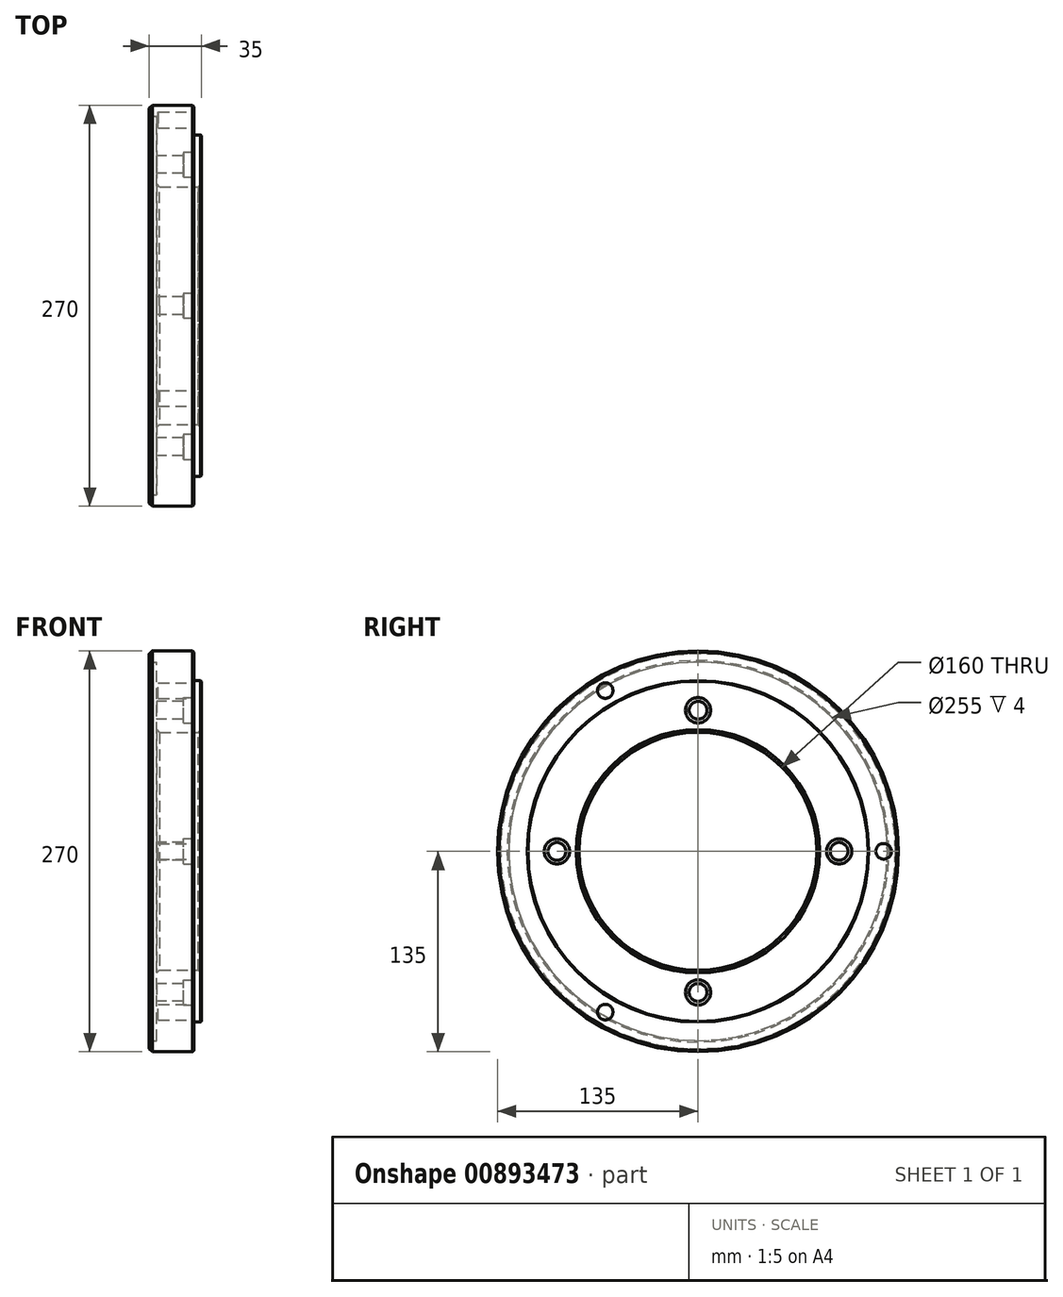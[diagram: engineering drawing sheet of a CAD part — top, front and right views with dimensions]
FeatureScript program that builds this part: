
annotation { "Feature Type Name" : "Feature", "Feature Type Description" : "" }
export const myFeature = defineFeature(function(context is Context, id is Id, definition is map)
    precondition{}
    {
        {
            var Q0;
            Q0=qCreatedBy(makeId("Top.planeOp"),FACE);
            var sketch = newSketch(context, id + "F0", { "sketchPlane" : qUnion([Q0])});
            skLineSegment(sketch, "E0", {"start": v(0, 0) * mm, "end": v(-84.67, 0) * mm, "construction": true});
            skLineSegment(sketch, "E1", {"start": v(0, 80) * mm, "end": v(0, 115) * mm});
            skLineSegment(sketch, "E2", {"start": v(0, 115) * mm, "end": v(-5, 115) * mm});
            skLineSegment(sketch, "E3", {"start": v(-5, 115) * mm, "end": v(-5, 135) * mm});
            skLineSegment(sketch, "E4", {"start": v(-5, 135) * mm, "end": v(-35, 135) * mm});
            skLineSegment(sketch, "E5", {"start": v(-35, 135) * mm, "end": v(-35, 127.5) * mm});
            skLineSegment(sketch, "E6", {"start": v(-35, 127.5) * mm, "end": v(-30, 127.5) * mm});
            skLineSegment(sketch, "E7", {"start": v(-30, 127.5) * mm, "end": v(-30, 80) * mm});
            skLineSegment(sketch, "E8", {"start": v(-30, 80) * mm, "end": v(0, 80) * mm});
            skSolve(sketch);
        }
        {
            var Q0;
            Q0=makeQuery(id+"F0.imprint","IMPRINT",FACE,{"disambiguationData":[TD([[makeQuery(id+"F0.imprint","IMPRINT",EDGE,{"derivedFrom":sQuery(id+"F0.wireOp",EDGE,"E1")}),1.0]])]});
            var Q1;
            Q1=sQuery(id+"F0.wireOp",EDGE,"E0");
            revolve(context, id + "F1", {"surfaceOperationType" : NewSurfaceOperationType.NEW, "entities" : qUnion([Q0]), "axis" : qUnion([Q1]), "revolveType" : RevolveType.FULL});
        }
        {
            var Q0;
            Q0=makeQuery(id+"F1.opRevolve","SWEPT_FACE",FACE,{"disambiguationData":[OSD([sQuery(id+"F0.wireOp",EDGE,"E7")])]});
            var sketch = newSketch(context, id + "F2", { "sketchPlane" : qUnion([Q0])});
            skLineSegment(sketch, "E9", {"start": v(0, 0) * mm, "end": v(-95, 0) * mm, "construction": true});
            skCircle(sketch, "E10", {"center": v(-95, 0) * mm, "radius": 6 * mm});
            skCircle(sketch, "E11.1.0", {"center": v(0, -95) * mm, "radius": 6 * mm});
            skCircle(sketch, "E11.2.0", {"center": v(95, 0) * mm, "radius": 6 * mm});
            skCircle(sketch, "E11.3.0", {"center": v(0, 95) * mm, "radius": 6 * mm});
            skPoint(sketch, "E11.center", {"position": v(0, 0) * mm});
            skSolve(sketch);
        }
        {
            var Q0;
            Q0 = qSketchRegion(id + "F2", true);
            extrude(context, id + "F3", {"entities" : qUnion([Q0]), "operationType" : NewBodyOperationType.REMOVE, "endBound" : BoundingType.THROUGH_ALL, "oppositeDirection" : true, "depth" : 25 * mm, "offsetDistance" : 25 * mm});
        }
        {
            var Q0;
            Q0=makeQuery(id+"F1.opRevolve","SWEPT_FACE",FACE,{"disambiguationData":[OSD([sQuery(id+"F0.wireOp",EDGE,"E1")])]});
            var sketch = newSketch(context, id + "F4", { "sketchPlane" : qUnion([Q0])});
            skCircle(sketch, "E12", {"center": v(0, -95) * mm, "radius": 8.5 * mm});
            skCircle(sketch, "E13.1.0", {"center": v(95, 0) * mm, "radius": 8.5 * mm});
            skCircle(sketch, "E13.2.0", {"center": v(0, 95) * mm, "radius": 8.5 * mm});
            skCircle(sketch, "E13.3.0", {"center": v(-95, 0) * mm, "radius": 8.5 * mm});
            skPoint(sketch, "E13.center", {"position": v(0, 0) * mm});
            skLineSegment(sketch, "E14", {"start": v(0, 0) * mm, "end": v(0, -95) * mm, "construction": true});
            skSolve(sketch);
        }
        {
            var Q0;
            Q0 = qSketchRegion(id + "F4", true);
            extrude(context, id + "F5", {"entities" : qUnion([Q0]), "operationType" : NewBodyOperationType.REMOVE, "oppositeDirection" : true, "depth" : 12 * mm, "offsetDistance" : 25 * mm});
        }
        {
            var Q0;
            Q0=makeQuery(id+"F1.opRevolve","SWEPT_FACE",FACE,{"disambiguationData":[OSD([sQuery(id+"F0.wireOp",EDGE,"E3")])]});
            var sketch = newSketch(context, id + "F6", { "sketchPlane" : qUnion([Q0])});
            skLineSegment(sketch, "E15", {"start": v(0, 0) * mm, "end": v(125, 0) * mm, "construction": true});
            skCircle(sketch, "E16", {"center": v(125, 0) * mm, "radius": 5.25 * mm});
            skCircle(sketch, "E17.1.0", {"center": v(-62.5, 108.25) * mm, "radius": 5.25 * mm});
            skCircle(sketch, "E17.2.0", {"center": v(-62.5, -108.25) * mm, "radius": 5.25 * mm});
            skPoint(sketch, "E17.center", {"position": v(0, 0) * mm});
            skSolve(sketch);
        }
        {
            var Q0;
            Q0 = qSketchRegion(id + "F6", true);
            var Q1;
            Q1=sQuery(id+"F6.wireOp",EDGE,"E16");
            extrude(context, id + "F7", {"entities" : qUnion([Q0]), "operationType" : NewBodyOperationType.REMOVE, "surfaceEntities" : qUnion([Q1]), "oppositeDirection" : true, "depth" : 24 * mm, "offsetDistance" : 25 * mm});
        }
        {
            var Q0;
            Q0=makeQuery(id+"F1.opRevolve","SWEPT_EDGE",EDGE,{"disambiguationData":[OSD([sQuery(id+"F0.wireOp",EDGE,"E7"),sQuery(id+"F0.wireOp",EDGE,"E8")])]});
            var Q1;
            Q1=makeQuery(id+"F1.opRevolve","SWEPT_EDGE",EDGE,{"disambiguationData":[OSD([sQuery(id+"F0.wireOp",EDGE,"E4"),sQuery(id+"F0.wireOp",EDGE,"E5")])]});
            var Q2;
            Q2=makeQuery(id+"F1.opRevolve","SWEPT_EDGE",EDGE,{"disambiguationData":[OSD([sQuery(id+"F0.wireOp",EDGE,"E1"),sQuery(id+"F0.wireOp",EDGE,"E8")])]});
            chamfer(context, id + "F8", {"entities" : qUnion([Q0, Q1, Q2]), "width" : 2 * mm, "tangentPropagation" : true});
        }
        {
            var Q0;
            Q0=makeQuery(id+"F1.opRevolve","SWEPT_EDGE",EDGE,{"disambiguationData":[OSD([sQuery(id+"F0.wireOp",EDGE,"E5"),sQuery(id+"F0.wireOp",EDGE,"E6")])]});
            var Q1;
            Q1=makeQuery(id+"F3.boolean.opBoolean","COPY",EDGE,{"derivedFrom":makeQuery(id+"F3.opExtrude","CAP_EDGE",EDGE,{"disambiguationData":[OSD([sQuery(id+"F2.wireOp",EDGE,"E11.1.0")])],"isStart":true})});
            var Q2;
            Q2=makeQuery(id+"F3.boolean.opBoolean","COPY",EDGE,{"derivedFrom":makeQuery(id+"F3.opExtrude","CAP_EDGE",EDGE,{"disambiguationData":[OSD([sQuery(id+"F2.wireOp",EDGE,"E10")])],"isStart":true})});
            var Q3;
            Q3=makeQuery(id+"F3.boolean.opBoolean","COPY",EDGE,{"derivedFrom":makeQuery(id+"F3.opExtrude","CAP_EDGE",EDGE,{"disambiguationData":[OSD([sQuery(id+"F2.wireOp",EDGE,"E11.3.0")])],"isStart":true})});
            var Q4;
            Q4=makeQuery(id+"F3.boolean.opBoolean","COPY",EDGE,{"derivedFrom":makeQuery(id+"F3.opExtrude","CAP_EDGE",EDGE,{"disambiguationData":[OSD([sQuery(id+"F2.wireOp",EDGE,"E11.2.0")])],"isStart":true})});
            var Q5;
            Q5=makeQuery(id+"F5.boolean.opBoolean","COPY",EDGE,{"derivedFrom":makeQuery(id+"F5.opExtrude","CAP_EDGE",EDGE,{"disambiguationData":[OSD([sQuery(id+"F4.wireOp",EDGE,"E13.2.0")])],"isStart":true})});
            var Q6;
            Q6=makeQuery(id+"F5.boolean.opBoolean","COPY",EDGE,{"derivedFrom":makeQuery(id+"F5.opExtrude","CAP_EDGE",EDGE,{"disambiguationData":[OSD([sQuery(id+"F4.wireOp",EDGE,"E13.1.0")])],"isStart":true})});
            var Q7;
            Q7=makeQuery(id+"F5.boolean.opBoolean","COPY",EDGE,{"derivedFrom":makeQuery(id+"F5.opExtrude","CAP_EDGE",EDGE,{"disambiguationData":[OSD([sQuery(id+"F4.wireOp",EDGE,"E12")])],"isStart":true})});
            var Q8;
            Q8=makeQuery(id+"F5.boolean.opBoolean","COPY",EDGE,{"derivedFrom":makeQuery(id+"F5.opExtrude","CAP_EDGE",EDGE,{"disambiguationData":[OSD([sQuery(id+"F4.wireOp",EDGE,"E13.3.0")])],"isStart":true})});
            var Q9;
            Q9=makeQuery(id+"F7.boolean.opBoolean","COPY",EDGE,{"derivedFrom":makeQuery(id+"F7.opExtrude","CAP_EDGE",EDGE,{"disambiguationData":[OSD([sQuery(id+"F6.wireOp",EDGE,"E16")])],"isStart":true})});
            var Q10;
            Q10=makeQuery(id+"F7.boolean.opBoolean","COPY",EDGE,{"derivedFrom":makeQuery(id+"F7.opExtrude","CAP_EDGE",EDGE,{"disambiguationData":[OSD([sQuery(id+"F6.wireOp",EDGE,"E17.1.0")])],"isStart":true})});
            var Q11;
            Q11=makeQuery(id+"F7.boolean.opBoolean","COPY",EDGE,{"derivedFrom":makeQuery(id+"F7.opExtrude","CAP_EDGE",EDGE,{"disambiguationData":[OSD([sQuery(id+"F6.wireOp",EDGE,"E17.2.0")])],"isStart":true})});
            var Q12;
            Q12=makeQuery(id+"F1.opRevolve","SWEPT_EDGE",EDGE,{"disambiguationData":[OSD([sQuery(id+"F0.wireOp",EDGE,"E3"),sQuery(id+"F0.wireOp",EDGE,"E4")])]});
            chamfer(context, id + "F9", {"entities" : qUnion([Q0, Q1, Q2, Q3, Q4, Q5, Q6, Q7, Q8, Q9, Q10, Q11, Q12]), "width" : 1 * mm, "tangentPropagation" : true});
        }
        {
            var Q0;
            Q0=makeQuery(id+"F1.opRevolve","SWEPT_EDGE",EDGE,{"disambiguationData":[OSD([sQuery(id+"F0.wireOp",EDGE,"E1"),sQuery(id+"F0.wireOp",EDGE,"E2")])]});
            chamfer(context, id + "F10", {"entities" : qUnion([Q0]), "width" : 0.5 * mm, "tangentPropagation" : true});
        }
    });
